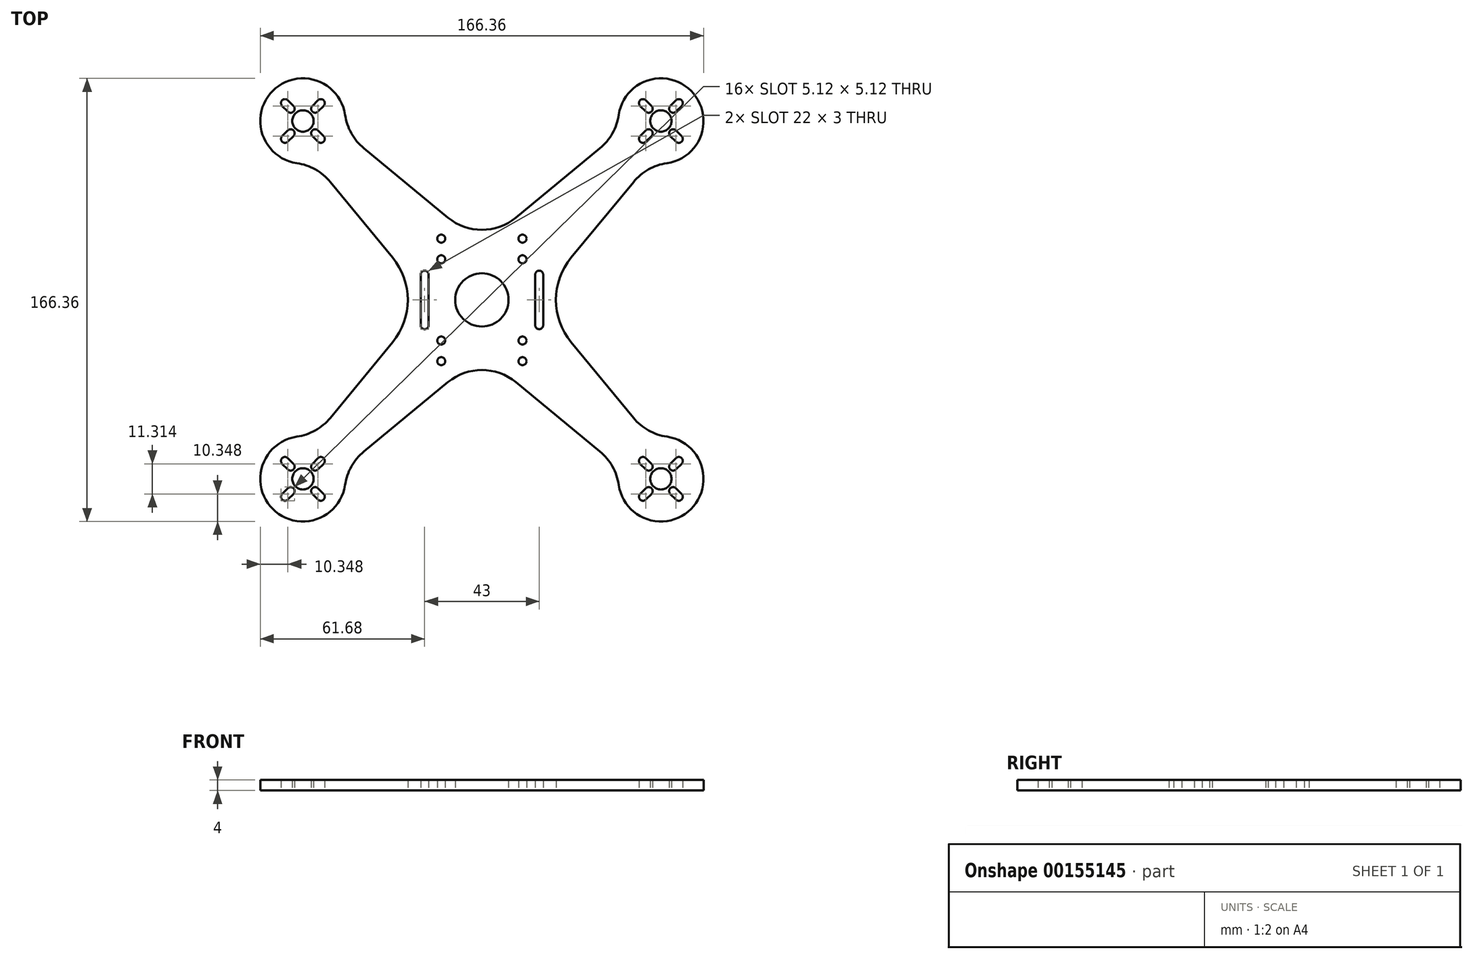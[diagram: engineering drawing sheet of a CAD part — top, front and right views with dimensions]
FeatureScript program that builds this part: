
annotation { "Feature Type Name" : "Feature", "Feature Type Description" : "" }
export const myFeature = defineFeature(function(context is Context, id is Id, definition is map)
    precondition{}
    {
        {
            var Q0;
            Q0=qCreatedBy(makeId("Top.planeOp"),FACE);
            var sketch = newSketch(context, id + "F0", { "sketchPlane" : qUnion([Q0])});
            skArc(sketch, "E0", {"start": v(0, 95) * mm, "mid": v(-67.18, 67.18) * mm, "end": v(-95, 0) * mm, "construction": true});
            skLineSegment(sketch, "E1", {"start": v(0, 0) * mm, "end": v(-67.18, 67.18) * mm, "construction": true});
            skCircle(sketch, "E2", {"center": v(-67.18, 67.18) * mm, "radius": 4 * mm});
            skArc(sketch, "E3", {"start": v(-51.34, 69.46) * mm, "mid": v(-78.49, 78.49) * mm, "end": v(-69.46, 51.34) * mm});
            skArc(sketch, "E4", {"start": v(-61.52, 63.64) * mm, "mid": v(-63.64, 63.64) * mm, "end": v(-63.64, 61.52) * mm});
            skArc(sketch, "E5", {"start": v(-61.52, 59.4) * mm, "mid": v(-59.4, 59.4) * mm, "end": v(-59.4, 61.52) * mm});
            skLineSegment(sketch, "E6", {"start": v(-63.64, 61.52) * mm, "end": v(-61.52, 59.4) * mm});
            skLineSegment(sketch, "E7", {"start": v(-61.52, 63.64) * mm, "end": v(-59.4, 61.52) * mm});
            skLineSegment(sketch, "E8.1.0", {"start": v(-63.64, 72.83) * mm, "end": v(-61.52, 74.95) * mm});
            skArc(sketch, "E8.1.1", {"start": v(-59.4, 72.83) * mm, "mid": v(-59.4, 74.95) * mm, "end": v(-61.52, 74.95) * mm});
            skLineSegment(sketch, "E8.1.2", {"start": v(-61.52, 70.71) * mm, "end": v(-59.4, 72.83) * mm});
            skArc(sketch, "E8.1.3", {"start": v(-63.64, 72.83) * mm, "mid": v(-63.64, 70.71) * mm, "end": v(-61.52, 70.71) * mm});
            skLineSegment(sketch, "E8.2.0", {"start": v(-72.83, 70.71) * mm, "end": v(-74.95, 72.83) * mm});
            skArc(sketch, "E8.2.1", {"start": v(-72.83, 74.95) * mm, "mid": v(-74.95, 74.95) * mm, "end": v(-74.95, 72.83) * mm});
            skLineSegment(sketch, "E8.2.2", {"start": v(-70.71, 72.83) * mm, "end": v(-72.83, 74.95) * mm});
            skArc(sketch, "E8.2.3", {"start": v(-72.83, 70.71) * mm, "mid": v(-70.71, 70.71) * mm, "end": v(-70.71, 72.83) * mm});
            skLineSegment(sketch, "E8.3.0", {"start": v(-70.71, 61.52) * mm, "end": v(-72.83, 59.4) * mm});
            skArc(sketch, "E8.3.1", {"start": v(-74.95, 61.52) * mm, "mid": v(-74.95, 59.4) * mm, "end": v(-72.83, 59.4) * mm});
            skLineSegment(sketch, "E8.3.2", {"start": v(-72.83, 63.64) * mm, "end": v(-74.95, 61.52) * mm});
            skArc(sketch, "E8.3.3", {"start": v(-70.71, 61.52) * mm, "mid": v(-70.71, 63.64) * mm, "end": v(-72.83, 63.64) * mm});
            skLineSegment(sketch, "E9", {"start": v(-56.89, 44.27) * mm, "end": v(-33.5, 15.9) * mm});
            skLineSegment(sketch, "E10", {"start": v(-44.27, 56.89) * mm, "end": v(-12.72, 30.89) * mm});
            skPoint(sketch, "E11.visualSharp", {"position": v(-63.03, 51.72) * mm});
            skArc(sketch, "E11.filletArc", {"start": v(-56.89, 44.27) * mm, "mid": v(-62.52, 48.98) * mm, "end": v(-69.46, 51.34) * mm});
            skPoint(sketch, "E12.visualSharp", {"position": v(-51.72, 63.03) * mm});
            skArc(sketch, "E12.filletArc", {"start": v(-51.34, 69.46) * mm, "mid": v(-48.98, 62.52) * mm, "end": v(-44.27, 56.89) * mm});
            skLineSegment(sketch, "E13", {"start": v(0, 0) * mm, "end": v(0, 95) * mm, "construction": true});
            skLineSegment(sketch, "E14", {"start": v(0, 0) * mm, "end": v(-95, 0) * mm, "construction": true});
            skCircle(sketch, "E15", {"center": v(-15.25, 15.25) * mm, "radius": 1.5 * mm});
            skCircle(sketch, "E16", {"center": v(-67.18, 67.18) * mm, "radius": 63.5 * mm, "construction": true});
            skArc(sketch, "E17.MirrorCS", {"start": v(70.71, 61.52) * mm, "mid": v(70.71, 63.64) * mm, "end": v(72.83, 63.64) * mm});
            skArc(sketch, "E18.MirrorCS", {"start": v(61.52, 63.64) * mm, "mid": v(63.64, 63.64) * mm, "end": v(63.64, 61.52) * mm});
            skLineSegment(sketch, "E19.MirrorCS", {"start": v(63.64, 61.52) * mm, "end": v(61.52, 59.4) * mm});
            skLineSegment(sketch, "E20.MirrorCS", {"start": v(61.52, 63.64) * mm, "end": v(59.4, 61.52) * mm});
            skLineSegment(sketch, "E21.MirrorCS", {"start": v(70.71, 61.52) * mm, "end": v(72.83, 59.4) * mm});
            skLineSegment(sketch, "E22.MirrorCS", {"start": v(72.83, 70.71) * mm, "end": v(74.95, 72.83) * mm});
            skLineSegment(sketch, "E23.MirrorCS", {"start": v(70.71, 72.83) * mm, "end": v(72.83, 74.95) * mm});
            skCircle(sketch, "E24.MirrorC", {"center": v(67.18, 67.18) * mm, "radius": 4 * mm});
            skArc(sketch, "E25.MirrorCS", {"start": v(61.52, 59.4) * mm, "mid": v(59.4, 59.4) * mm, "end": v(59.4, 61.52) * mm});
            skLineSegment(sketch, "E26.MirrorCS", {"start": v(63.64, 72.83) * mm, "end": v(61.52, 74.95) * mm});
            skArc(sketch, "E27.MirrorCS", {"start": v(59.4, 72.83) * mm, "mid": v(59.4, 74.95) * mm, "end": v(61.52, 74.95) * mm});
            skLineSegment(sketch, "E28.MirrorCS", {"start": v(61.52, 70.71) * mm, "end": v(59.4, 72.83) * mm});
            skArc(sketch, "E29.MirrorCS", {"start": v(63.64, 72.83) * mm, "mid": v(63.64, 70.71) * mm, "end": v(61.52, 70.71) * mm});
            skLineSegment(sketch, "E30.MirrorCS", {"start": v(72.83, 63.64) * mm, "end": v(74.95, 61.52) * mm});
            skArc(sketch, "E31.MirrorCS", {"start": v(74.95, 61.52) * mm, "mid": v(74.95, 59.4) * mm, "end": v(72.83, 59.4) * mm});
            skArc(sketch, "E32.MirrorCS", {"start": v(72.83, 74.95) * mm, "mid": v(74.95, 74.95) * mm, "end": v(74.95, 72.83) * mm});
            skArc(sketch, "E33.MirrorCS", {"start": v(72.83, 70.71) * mm, "mid": v(70.71, 70.71) * mm, "end": v(70.71, 72.83) * mm});
            skArc(sketch, "E34.MirrorCS", {"start": v(51.34, 69.46) * mm, "mid": v(48.98, 62.52) * mm, "end": v(44.27, 56.89) * mm});
            skCircle(sketch, "E35.MirrorC", {"center": v(15.25, 15.25) * mm, "radius": 1.5 * mm});
            skArc(sketch, "E36.MirrorCS", {"start": v(56.89, 44.27) * mm, "mid": v(62.52, 48.98) * mm, "end": v(69.46, 51.34) * mm});
            skCircle(sketch, "E37.MirrorC", {"center": v(67.18, 67.18) * mm, "radius": 63.5 * mm, "construction": true});
            skLineSegment(sketch, "E38.MirrorCS", {"start": v(0, 0) * mm, "end": v(95, 0) * mm, "construction": true});
            skLineSegment(sketch, "E39.MirrorCS", {"start": v(44.27, 56.89) * mm, "end": v(12.72, 30.89) * mm});
            skArc(sketch, "E40.MirrorCS", {"start": v(0, 95) * mm, "mid": v(67.18, 67.18) * mm, "end": v(95, 0) * mm, "construction": true});
            skLineSegment(sketch, "E41.MirrorCS", {"start": v(0, 0) * mm, "end": v(67.18, 67.18) * mm, "construction": true});
            skArc(sketch, "E42.MirrorCS", {"start": v(51.34, 69.46) * mm, "mid": v(78.49, 78.49) * mm, "end": v(69.46, 51.34) * mm});
            skPoint(sketch, "E43.MirrorP", {"position": v(51.72, 63.03) * mm});
            skLineSegment(sketch, "E44.MirrorCS", {"start": v(56.89, 44.27) * mm, "end": v(33.5, 15.9) * mm});
            skPoint(sketch, "E45.MirrorP", {"position": v(63.03, 51.72) * mm});
            skArc(sketch, "E46.MirrorCS", {"start": v(72.83, -74.95) * mm, "mid": v(74.95, -74.95) * mm, "end": v(74.95, -72.83) * mm});
            skArc(sketch, "E47.MirrorCS", {"start": v(61.52, -63.64) * mm, "mid": v(63.64, -63.64) * mm, "end": v(63.64, -61.52) * mm});
            skLineSegment(sketch, "E48.MirrorCS", {"start": v(-70.71, -72.83) * mm, "end": v(-72.83, -74.95) * mm});
            skLineSegment(sketch, "E49.MirrorCS", {"start": v(-61.52, -63.64) * mm, "end": v(-59.4, -61.52) * mm});
            skLineSegment(sketch, "E50.MirrorCS", {"start": v(-63.64, -61.52) * mm, "end": v(-61.52, -59.4) * mm});
            skArc(sketch, "E51.MirrorCS", {"start": v(-61.52, -63.64) * mm, "mid": v(-63.64, -63.64) * mm, "end": v(-63.64, -61.52) * mm});
            skArc(sketch, "E52.MirrorCS", {"start": v(-72.83, -70.71) * mm, "mid": v(-70.71, -70.71) * mm, "end": v(-70.71, -72.83) * mm});
            skArc(sketch, "E53.MirrorCS", {"start": v(61.52, -59.4) * mm, "mid": v(59.4, -59.4) * mm, "end": v(59.4, -61.52) * mm});
            skLineSegment(sketch, "E54.MirrorCS", {"start": v(70.71, -61.52) * mm, "end": v(72.83, -59.4) * mm});
            skArc(sketch, "E55.MirrorCS", {"start": v(72.83, -70.71) * mm, "mid": v(70.71, -70.71) * mm, "end": v(70.71, -72.83) * mm});
            skArc(sketch, "E56.MirrorCS", {"start": v(70.71, -61.52) * mm, "mid": v(70.71, -63.64) * mm, "end": v(72.83, -63.64) * mm});
            skLineSegment(sketch, "E57.MirrorCS", {"start": v(63.64, -61.52) * mm, "end": v(61.52, -59.4) * mm});
            skLineSegment(sketch, "E58.MirrorCS", {"start": v(72.83, -70.71) * mm, "end": v(74.95, -72.83) * mm});
            skLineSegment(sketch, "E59.MirrorCS", {"start": v(72.83, -63.64) * mm, "end": v(74.95, -61.52) * mm});
            skLineSegment(sketch, "E60.MirrorCS", {"start": v(61.52, -63.64) * mm, "end": v(59.4, -61.52) * mm});
            skLineSegment(sketch, "E61.MirrorCS", {"start": v(70.71, -72.83) * mm, "end": v(72.83, -74.95) * mm});
            skArc(sketch, "E62.MirrorCS", {"start": v(-72.83, -74.95) * mm, "mid": v(-74.95, -74.95) * mm, "end": v(-74.95, -72.83) * mm});
            skArc(sketch, "E63.MirrorCS", {"start": v(-70.71, -61.52) * mm, "mid": v(-70.71, -63.64) * mm, "end": v(-72.83, -63.64) * mm});
            skLineSegment(sketch, "E64.MirrorCS", {"start": v(-72.83, -70.71) * mm, "end": v(-74.95, -72.83) * mm});
            skArc(sketch, "E65.MirrorCS", {"start": v(-63.64, -72.83) * mm, "mid": v(-63.64, -70.71) * mm, "end": v(-61.52, -70.71) * mm});
            skLineSegment(sketch, "E66.MirrorCS", {"start": v(-61.52, -70.71) * mm, "end": v(-59.4, -72.83) * mm});
            skLineSegment(sketch, "E67.MirrorCS", {"start": v(-63.64, -72.83) * mm, "end": v(-61.52, -74.95) * mm});
            skArc(sketch, "E68.MirrorCS", {"start": v(-61.52, -59.4) * mm, "mid": v(-59.4, -59.4) * mm, "end": v(-59.4, -61.52) * mm});
            skCircle(sketch, "E69.MirrorC", {"center": v(67.18, -67.18) * mm, "radius": 4 * mm});
            skArc(sketch, "E70.MirrorCS", {"start": v(74.95, -61.52) * mm, "mid": v(74.95, -59.4) * mm, "end": v(72.83, -59.4) * mm});
            skCircle(sketch, "E71.MirrorC", {"center": v(-67.18, -67.18) * mm, "radius": 4 * mm});
            skLineSegment(sketch, "E72.MirrorCS", {"start": v(-70.71, -61.52) * mm, "end": v(-72.83, -59.4) * mm});
            skArc(sketch, "E73.MirrorCS", {"start": v(-74.95, -61.52) * mm, "mid": v(-74.95, -59.4) * mm, "end": v(-72.83, -59.4) * mm});
            skLineSegment(sketch, "E74.MirrorCS", {"start": v(-72.83, -63.64) * mm, "end": v(-74.95, -61.52) * mm});
            skArc(sketch, "E75.MirrorCS", {"start": v(51.34, -69.46) * mm, "mid": v(48.98, -62.52) * mm, "end": v(44.27, -56.89) * mm});
            skArc(sketch, "E76.MirrorCS", {"start": v(-51.34, -69.46) * mm, "mid": v(-48.98, -62.52) * mm, "end": v(-44.27, -56.89) * mm});
            skLineSegment(sketch, "E77.MirrorCS", {"start": v(61.52, -70.71) * mm, "end": v(59.4, -72.83) * mm});
            skArc(sketch, "E78.MirrorCS", {"start": v(-59.4, -72.83) * mm, "mid": v(-59.4, -74.95) * mm, "end": v(-61.52, -74.95) * mm});
            skArc(sketch, "E79.MirrorCS", {"start": v(63.64, -72.83) * mm, "mid": v(63.64, -70.71) * mm, "end": v(61.52, -70.71) * mm});
            skLineSegment(sketch, "E80.MirrorCS", {"start": v(63.64, -72.83) * mm, "end": v(61.52, -74.95) * mm});
            skArc(sketch, "E81.MirrorCS", {"start": v(-56.89, -44.27) * mm, "mid": v(-62.52, -48.98) * mm, "end": v(-69.46, -51.34) * mm});
            skArc(sketch, "E82.MirrorCS", {"start": v(56.89, -44.27) * mm, "mid": v(62.52, -48.98) * mm, "end": v(69.46, -51.34) * mm});
            skArc(sketch, "E83.MirrorCS", {"start": v(59.4, -72.83) * mm, "mid": v(59.4, -74.95) * mm, "end": v(61.52, -74.95) * mm});
            skCircle(sketch, "E84.MirrorC", {"center": v(-15.25, -15.25) * mm, "radius": 1.5 * mm});
            skCircle(sketch, "E85.MirrorC", {"center": v(15.25, -15.25) * mm, "radius": 1.5 * mm});
            skArc(sketch, "E86.MirrorCS", {"start": v(0, -95) * mm, "mid": v(-67.18, -67.18) * mm, "end": v(-95, 0) * mm, "construction": true});
            skCircle(sketch, "E87.MirrorC", {"center": v(-67.18, -67.18) * mm, "radius": 63.5 * mm, "construction": true});
            skArc(sketch, "E88.MirrorCS", {"start": v(-51.34, -69.46) * mm, "mid": v(-78.49, -78.49) * mm, "end": v(-69.46, -51.34) * mm});
            skLineSegment(sketch, "E89.MirrorCS", {"start": v(0, 0) * mm, "end": v(67.18, -67.18) * mm, "construction": true});
            skLineSegment(sketch, "E90.MirrorCS", {"start": v(0, 0) * mm, "end": v(-67.18, -67.18) * mm, "construction": true});
            skArc(sketch, "E91.MirrorCS", {"start": v(0, -95) * mm, "mid": v(67.18, -67.18) * mm, "end": v(95, 0) * mm, "construction": true});
            skLineSegment(sketch, "E92.MirrorCS", {"start": v(-56.89, -44.27) * mm, "end": v(-33.5, -15.9) * mm});
            skPoint(sketch, "E93.MirrorP", {"position": v(-51.72, -63.03) * mm});
            skPoint(sketch, "E94.MirrorP", {"position": v(51.72, -63.03) * mm});
            skCircle(sketch, "E95.MirrorC", {"center": v(67.18, -67.18) * mm, "radius": 63.5 * mm, "construction": true});
            skPoint(sketch, "E96.MirrorP", {"position": v(63.03, -51.72) * mm});
            skPoint(sketch, "E97.MirrorP", {"position": v(-63.03, -51.72) * mm});
            skLineSegment(sketch, "E98.MirrorCS", {"start": v(0, 0) * mm, "end": v(0, -95) * mm, "construction": true});
            skLineSegment(sketch, "E99.MirrorCS", {"start": v(-44.27, -56.89) * mm, "end": v(-12.72, -30.89) * mm});
            skArc(sketch, "E100.MirrorCS", {"start": v(51.34, -69.46) * mm, "mid": v(78.49, -78.49) * mm, "end": v(69.46, -51.34) * mm});
            skLineSegment(sketch, "E101.MirrorCS", {"start": v(56.89, -44.27) * mm, "end": v(33.5, -15.9) * mm});
            skLineSegment(sketch, "E102.MirrorCS", {"start": v(44.27, -56.89) * mm, "end": v(12.72, -30.89) * mm});
            skPoint(sketch, "E103.visualSharp", {"position": v(0, 20.4) * mm});
            skArc(sketch, "E103.filletArc", {"start": v(-12.72, 30.89) * mm, "mid": v(0, 26.32) * mm, "end": v(12.72, 30.89) * mm});
            skPoint(sketch, "E104.visualSharp", {"position": v(0, -20.4) * mm});
            skArc(sketch, "E104.filletArc", {"start": v(12.72, -30.89) * mm, "mid": v(0, -26.32) * mm, "end": v(-12.72, -30.89) * mm});
            skPoint(sketch, "E105.visualSharp", {"position": v(-20.4, 0) * mm});
            skArc(sketch, "E105.filletArc", {"start": v(-33.5, -15.9) * mm, "mid": v(-27.8, 0) * mm, "end": v(-33.5, 15.9) * mm});
            skArc(sketch, "E106.filletArc", {"start": v(33.5, 15.9) * mm, "mid": v(27.8, 0) * mm, "end": v(33.5, -15.9) * mm});
            skLineSegment(sketch, "E107.left", {"start": v(-23, 9.5) * mm, "end": v(-23, -9.5) * mm});
            skLineSegment(sketch, "E107.right", {"start": v(-20, 9.5) * mm, "end": v(-20, -9.5) * mm});
            skArc(sketch, "E108", {"start": v(-20, 9.5) * mm, "mid": v(-21.5, 11) * mm, "end": v(-23, 9.5) * mm});
            skArc(sketch, "E109", {"start": v(-23, -9.5) * mm, "mid": v(-21.5, -11) * mm, "end": v(-20, -9.5) * mm});
            skPoint(sketch, "E110.1.0.0", {"position": v(22.6, 0) * mm});
            skLineSegment(sketch, "E110.1.0.1", {"start": v(23, 9.5) * mm, "end": v(23, -9.5) * mm});
            skArc(sketch, "E110.1.0.2", {"start": v(20, -9.5) * mm, "mid": v(21.5, -11) * mm, "end": v(23, -9.5) * mm});
            skLineSegment(sketch, "E110.1.0.3", {"start": v(20, 9.5) * mm, "end": v(20, -9.5) * mm});
            skArc(sketch, "E110.1.0.4", {"start": v(23, 9.5) * mm, "mid": v(21.5, 11) * mm, "end": v(20, 9.5) * mm});
            skLineSegment(sketch, "E110.direction1", {"start": v(-23, -9.5) * mm, "end": v(20, -9.5) * mm, "construction": true});
            skCircle(sketch, "E111", {"center": v(0, 0) * mm, "radius": 10 * mm});
            skCircle(sketch, "E112", {"center": v(-15.25, 23) * mm, "radius": 1.5 * mm});
            skCircle(sketch, "E113.0.1.0", {"center": v(-15.25, -23) * mm, "radius": 1.5 * mm});
            skCircle(sketch, "E113.1.0.0", {"center": v(15.25, 23) * mm, "radius": 1.5 * mm});
            skCircle(sketch, "E113.1.1.0", {"center": v(15.25, -23) * mm, "radius": 1.5 * mm});
            skLineSegment(sketch, "E113.direction1", {"start": v(-15.25, 23) * mm, "end": v(15.25, 23) * mm, "construction": true});
            skLineSegment(sketch, "E113.direction2", {"start": v(-15.25, 23) * mm, "end": v(-15.25, -23) * mm, "construction": true});
            skLineSegment(sketch, "E114.direction1", {"start": v(-23, -9.5) * mm, "end": v(-16.75, -9.5) * mm, "construction": true});
            skLineSegment(sketch, "E115.direction1", {"start": v(20, -9.5) * mm, "end": v(13.75, -9.5) * mm, "construction": true});
            skSolve(sketch);
        }
        {
            var Q0;
            Q0=makeQuery(id+"F0.imprint","IMPRINT",FACE,{"disambiguationData":[TD([[makeQuery(id+"F0.imprint","IMPRINT",EDGE,{"derivedFrom":sQuery(id+"F0.wireOp",EDGE,"E2")}),-1.0]])]});
            extrude(context, id + "F1", {"entities" : qUnion([Q0]), "depth" : 4 * mm});
        }
    });
